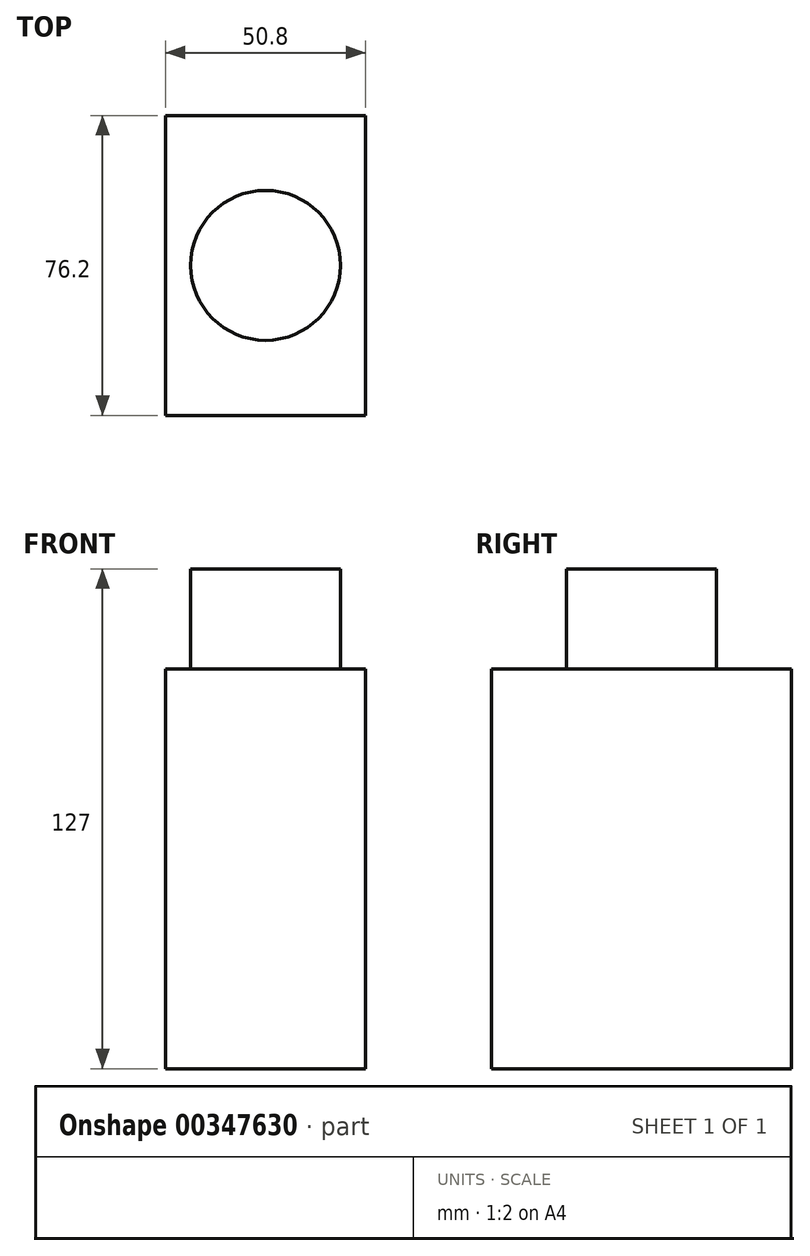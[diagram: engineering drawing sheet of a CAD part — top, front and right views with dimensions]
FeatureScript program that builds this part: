
annotation { "Feature Type Name" : "Feature", "Feature Type Description" : "" }
export const myFeature = defineFeature(function(context is Context, id is Id, definition is map)
    precondition{}
    {
        {
            var Q0;
            Q0=qCreatedBy(makeId("Front.planeOp"),FACE);
            var sketch = newSketch(context, id + "F0", { "sketchPlane" : qUnion([Q0])});
            skLineSegment(sketch, "E0", {"start": v(25.4, 25.4) * mm, "end": v(-25.4, 25.4) * mm});
            skLineSegment(sketch, "E1", {"start": v(-25.4, 25.4) * mm, "end": v(-25.4, 25.4) * mm});
            skLineSegment(sketch, "E2", {"start": v(-25.4, -76.2) * mm, "end": v(-25.4, 25.4) * mm});
            skLineSegment(sketch, "E3", {"start": v(-25.4, -76.2) * mm, "end": v(25.4, -76.2) * mm});
            skLineSegment(sketch, "E4", {"start": v(25.4, 25.4) * mm, "end": v(25.4, -76.2) * mm});
            skSolve(sketch);
        }
        {
            var Q0;
            Q0=makeQuery(id+"F0.imprint","IMPRINT",FACE,{"disambiguationData":[TD([[makeQuery(id+"F0.imprint","IMPRINT",EDGE,{"derivedFrom":sQuery(id+"F0.wireOp",EDGE,"E0")}),1.0]])]});
            extrude(context, id + "F1", {"entities" : qUnion([Q0]), "endBound" : BoundingType.SYMMETRIC, "depth" : 76.2 * mm});
        }
        {
            var Q0;
            Q0=makeQuery(id+"F1.opExtrude","SWEPT_FACE",FACE,{"disambiguationData":[OSD([sQuery(id+"F0.wireOp",EDGE,"E0")])]});
            var sketch = newSketch(context, id + "F2", { "sketchPlane" : qUnion([Q0])});
            skCircle(sketch, "E5", {"center": v(0, 0) * mm, "radius": 19.05 * mm});
            skSolve(sketch);
        }
        {
            var Q0;
            Q0 = qSketchRegion(id + "F2", true);
            var Q1;
            Q1=makeQuery(id+"F2.imprint","IMPRINT",FACE,{"disambiguationData":[TD([[makeQuery(id+"F2.imprint","IMPRINT",EDGE,{"derivedFrom":sQuery(id+"F2.wireOp",EDGE,"E5")}),1.0]])]});
            extrude(context, id + "F3", {"entities" : qUnion([Q0, Q1]), "operationType" : NewBodyOperationType.ADD, "depth" : 25.4 * mm});
        }
    });
